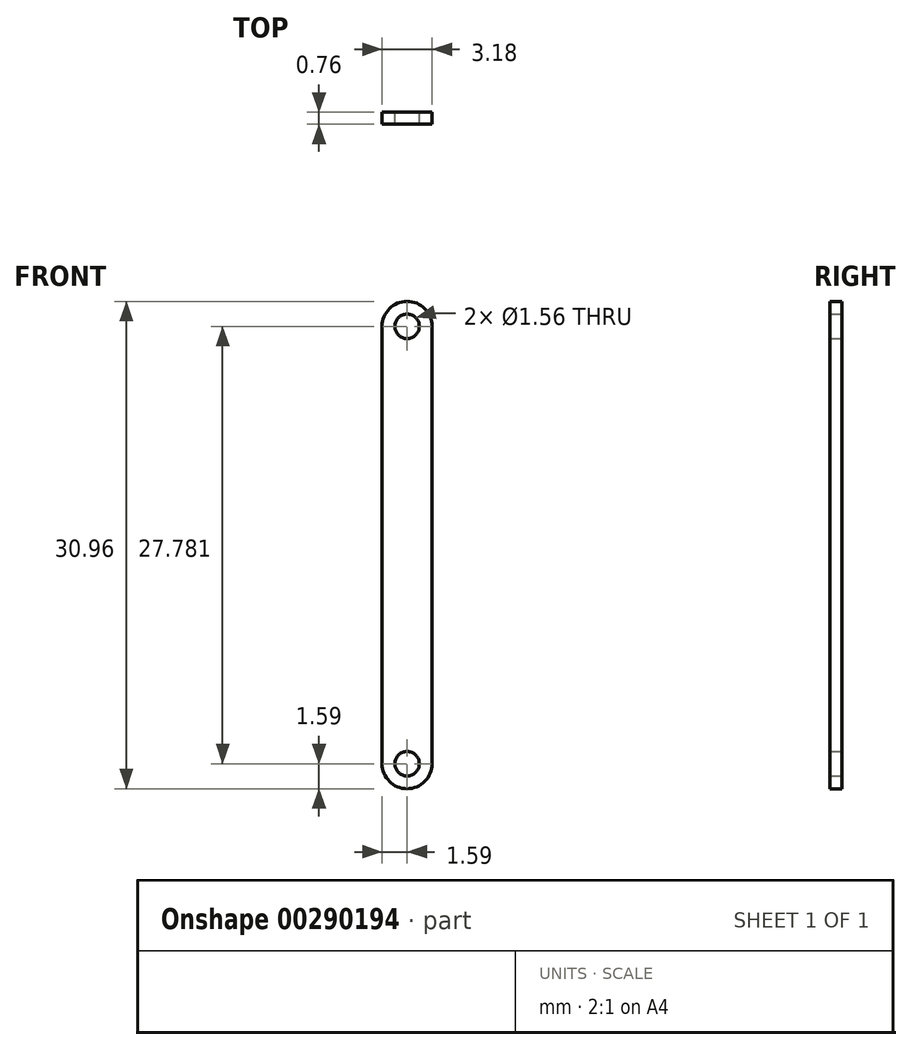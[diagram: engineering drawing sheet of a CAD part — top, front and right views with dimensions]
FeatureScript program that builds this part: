
annotation { "Feature Type Name" : "Feature", "Feature Type Description" : "" }
export const myFeature = defineFeature(function(context is Context, id is Id, definition is map)
    precondition{}
    {
        {
            var Q0;
            Q0=qCreatedBy(makeId("Front.planeOp"),FACE);
            var sketch = newSketch(context, id + "F0", { "sketchPlane" : qUnion([Q0])});
            skLineSegment(sketch, "E0", {"start": v(0, 0) * mm, "end": v(0, 27.78) * mm, "construction": true});
            skArc(sketch, "E1.0.startCap", {"start": v(1.59, 0) * mm, "mid": v(0, -1.59) * mm, "end": v(-1.59, 0) * mm});
            skArc(sketch, "E1.0.endCap", {"start": v(-1.59, 27.78) * mm, "mid": v(0, 29.37) * mm, "end": v(1.59, 27.78) * mm});
            skLineSegment(sketch, "E1.0.left", {"start": v(-1.59, 0) * mm, "end": v(-1.59, 27.78) * mm});
            skLineSegment(sketch, "E1.0.right", {"start": v(1.59, 0) * mm, "end": v(1.59, 27.78) * mm});
            skCircle(sketch, "E2", {"center": v(0, 0) * mm, "radius": 0.78 * mm});
            skCircle(sketch, "E3", {"center": v(0, 27.78) * mm, "radius": 0.78 * mm});
            skSolve(sketch);
        }
        {
            var Q0;
            Q0 = qSketchRegion(id + "F0", true);
            extrude(context, id + "F1", {"entities" : qUnion([Q0]), "endBound" : BoundingType.SYMMETRIC, "depth" : 0.76 * mm});
        }
    });
